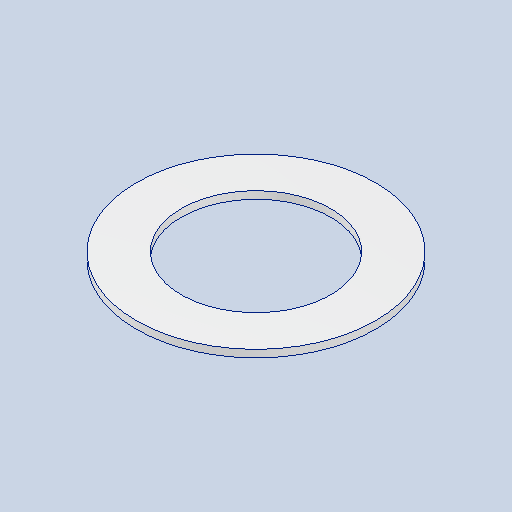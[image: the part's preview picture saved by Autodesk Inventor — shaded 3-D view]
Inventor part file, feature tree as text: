
AUTODESK INVENTOR PART (.ipt)
format: ipt  version: 2023 (Build 270158030, 158C)  size: 225,280 bytes
history: native  units: in
note: dims shown in document units (in); Inventor stores cm internally (conversion verified against a paired STEP export)
features: extrude x1, sketch x1
ambient origin geometry x8: Origin, YZ Plane, XZ Plane, XY Plane, X Axis, Y Axis, Z Axis, Center Point
bodies: Solid1 (feature_tree)
feature tree (2):
  extrude  "Extrusion1"  Depth=0.0197in
  sketch  "Sketch2"  dims[d0=0.3937in d1=0.6299in d2=0.0197in d3=0.0in]
